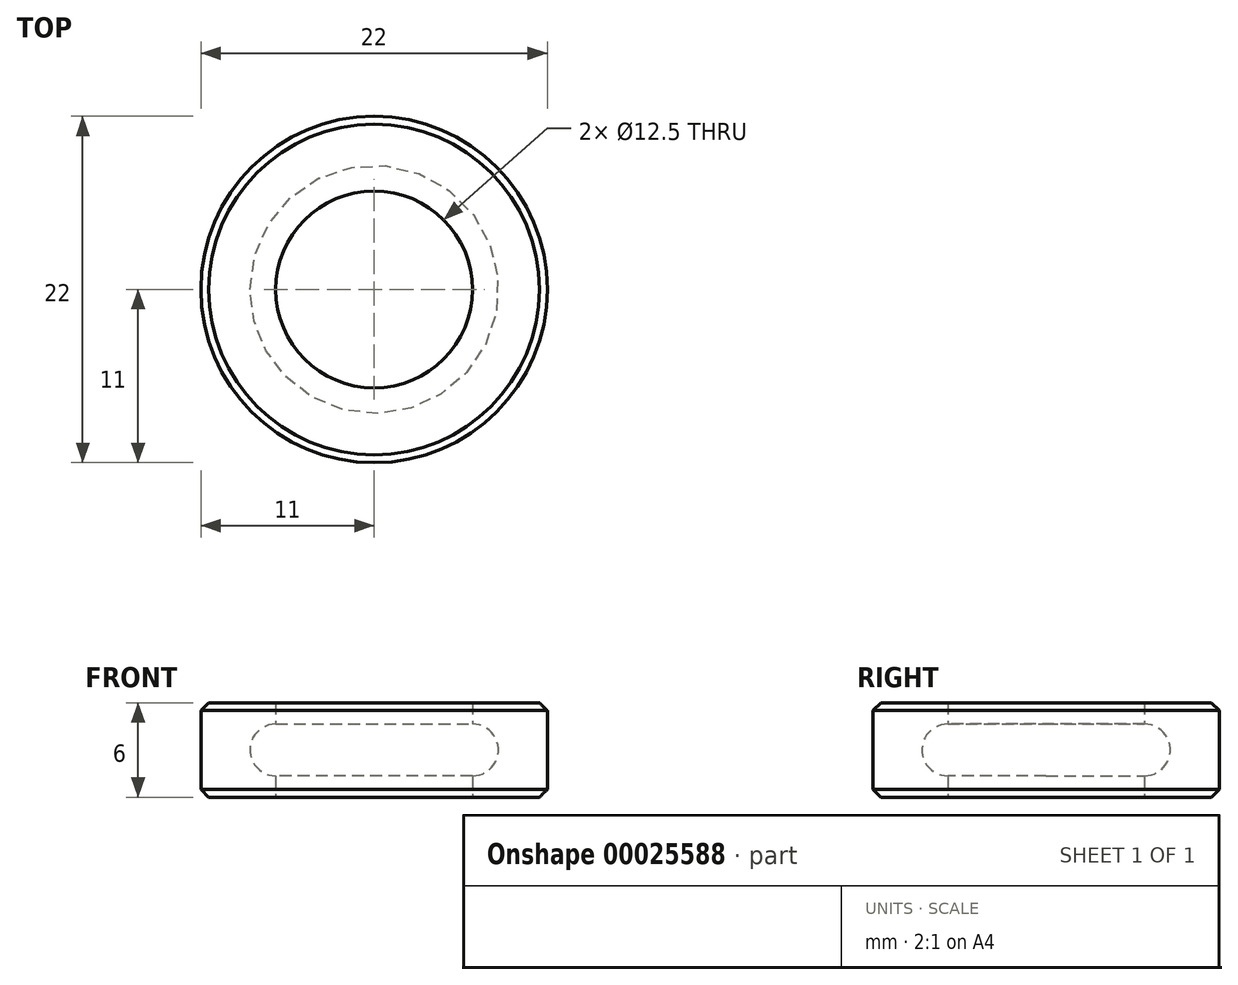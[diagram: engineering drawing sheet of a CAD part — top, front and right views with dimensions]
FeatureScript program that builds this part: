
annotation { "Feature Type Name" : "Feature", "Feature Type Description" : "" }
export const myFeature = defineFeature(function(context is Context, id is Id, definition is map)
    precondition{}
    {
        {
            var Q0;
            Q0=qCreatedBy(makeId("Top.planeOp"),FACE);
            var sketch = newSketch(context, id + "F0", { "sketchPlane" : qUnion([Q0])});
            skCircle(sketch, "E0", {"center": v(0, 0) * mm, "radius": 11 * mm});
            skCircle(sketch, "E1", {"center": v(0, 0) * mm, "radius": 6.25 * mm});
            skSolve(sketch);
        }
        {
            var Q0;
            Q0=makeQuery(id+"F0.imprint","IMPRINT",FACE,{"disambiguationData":[TD([[makeQuery(id+"F0.imprint","IMPRINT",EDGE,{"derivedFrom":sQuery(id+"F0.wireOp",EDGE,"E0")}),1.0]])]});
            extrude(context, id + "F1", {"entities" : qUnion([Q0]), "depth" : 6 * mm});
        }
        {
            var Q0;
            Q0=qCreatedBy(makeId("Front.planeOp"),FACE);
            var sketch = newSketch(context, id + "F2", { "sketchPlane" : qUnion([Q0])});
            skLineSegment(sketch, "E2.0", {"start": v(-6.25, 6) * mm, "end": v(6.25, 6) * mm, "construction": true});
            skLineSegment(sketch, "E3.0", {"start": v(-6.25, 0) * mm, "end": v(6.25, 0) * mm, "construction": true});
            skLineSegment(sketch, "E4", {"start": v(-6.25, 6) * mm, "end": v(-6.25, 0) * mm, "construction": true});
            skCircle(sketch, "E5", {"center": v(-6.25, 3) * mm, "radius": 1.64 * mm});
            skLineSegment(sketch, "E6", {"start": v(0, 6) * mm, "end": v(0, 0) * mm, "construction": true});
            skSolve(sketch);
        }
        {
            var Q0;
            Q0=makeQuery(id+"F2.imprint","IMPRINT",FACE,{"disambiguationData":[TD([[makeQuery(id+"F2.imprint","IMPRINT",EDGE,{"derivedFrom":sQuery(id+"F2.wireOp",EDGE,"E5")}),1.0]])]});
            var Q1;
            Q1=sQuery(id+"F2.wireOp",EDGE,"E6");
            revolve(context, id + "F3", {"operationType" : NewBodyOperationType.REMOVE, "entities" : qUnion([Q0]), "axis" : qUnion([Q1]), "revolveType" : RevolveType.FULL, "oppositeDirection" : true});
        }
        {
            var Q0;
            Q0=makeQuery(id+"F1.opExtrude","CAP_EDGE",EDGE,{"disambiguationData":[OSD([sQuery(id+"F0.wireOp",EDGE,"E0")])],"isStart":true});
            var Q1;
            Q1=makeQuery(id+"F1.opExtrude","CAP_EDGE",EDGE,{"disambiguationData":[OSD([sQuery(id+"F0.wireOp",EDGE,"E0")])],"isStart":false});
            chamfer(context, id + "F4", {"entities" : qUnion([Q0, Q1]), "width" : 0.5 * mm, "tangentPropagation" : true});
        }
    });
